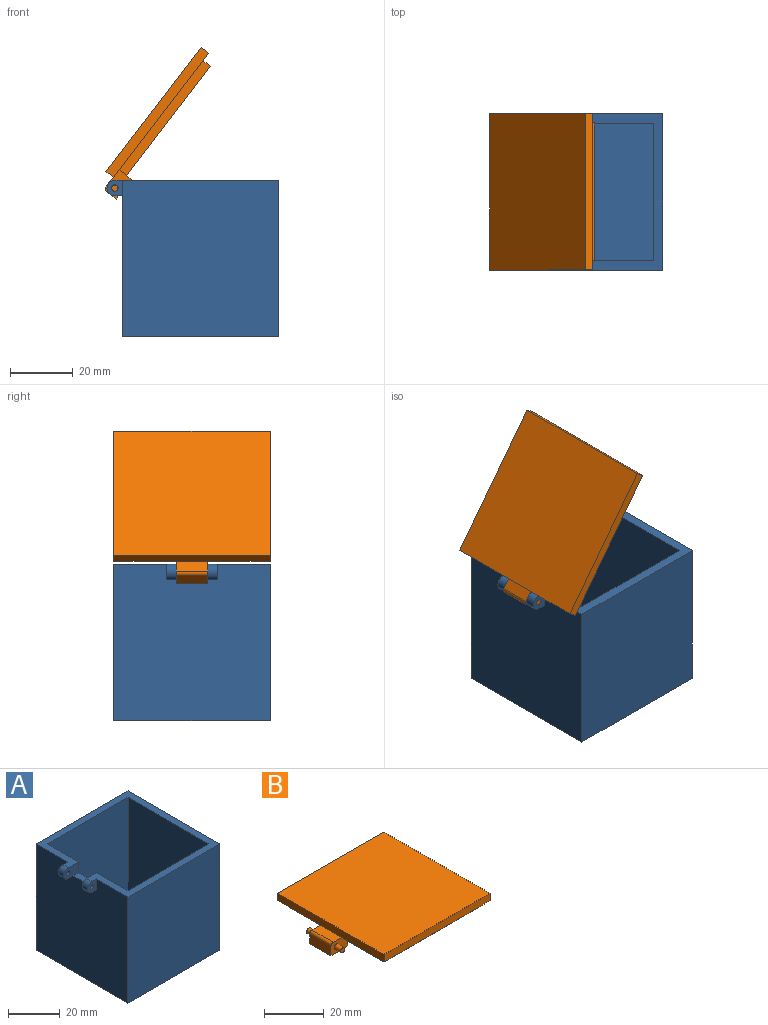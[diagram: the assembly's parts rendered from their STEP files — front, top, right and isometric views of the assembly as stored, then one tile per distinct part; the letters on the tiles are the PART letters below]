
ASSEMBLY  parts=2 mates=1
PART A: 22 faces, bbox 55x50x50 mm
  f0: plane 8x5mm, normal (0,-1,0), area 33.9mm2, adj f3,f4,f7,f16,f18,f21
  f1: plane 8x5mm, normal (0,1,0), area 33.9mm2, adj f3,f5,f7,f16,f19,f20
  f2: plane 5x5mm, normal (0,1,0), area 18.9mm2, adj f3,f4,f6,f18,f21
  f3: plane 52.5x50mm, normal (0,0,1), area 549mm2, adj f0,f1,f2,f6,f7,f8,f9,f10
  f4: plane 3x2.5mm, normal (0,0,-1), area 7.5mm2, adj f0,f2,f6,f18
  f5: plane 3x2.5mm, normal (0,0,-1), area 7.5mm2, adj f1,f6,f17,f19
  f6: plane 50x50mm, normal (-1,0,0), area 2420mm2, adj f2,f3,f4,f5,f8,f10,f11,f16
  f7: plane 47x44mm, normal (1,0,0), area 2018mm2, adj f0,f1,f3,f12,f14,f15,f16
  f8: plane 50x50mm, normal (0,-1,0), area 2500mm2, adj f3,f6,f9,f11
  f9: plane 50x50mm, normal (1,0,0), area 2500mm2, adj f3,f8,f10,f11
  f10: plane 50x50mm, normal (0,1,0), area 2500mm2, adj f3,f6,f9,f11
  f11: plane 50x50mm, normal (0,0,-1), area 2500mm2, adj f6,f8,f9,f10
  f12: plane 47x44mm, normal (0,1,0), area 2068mm2, adj f3,f7,f13,f15
  f13: plane 47x44mm, normal (-1,0,0), area 2068mm2, adj f3,f12,f14,f15
  f14: plane 47x44mm, normal (0,-1,0), area 2068mm2, adj f3,f7,f13,f15
  f15: plane 44x44mm, normal (0,0,1), area 1936mm2, adj f7,f12,f13,f14
  f16: plane 10x3mm, normal (0,0,1), area 30mm2, adj f0,f1,f6,f7
  f17: plane 5x5mm, normal (0,-1,0), area 18.9mm2, adj f3,f5,f6,f19,f20
  f18: cylinder r=2.5mm len=5mm, axis (0,-1,0), area 23.6mm2, adj f0,f2,f3,f4
  f19: cylinder r=2.5mm len=5mm, axis (0,-1,0), area 23.6mm2, adj f1,f3,f5,f17
  f20: cylinder r=1.05mm len=3mm, axis (0,-1,0), area 19.8mm2, adj f1,f17
  f21: cylinder r=1.05mm len=3mm, axis (0,-1,0), area 19.8mm2, adj f0,f2
PART B: 23 faces, bbox 55x50x8 mm
  f0: plane 17x3mm, normal (-1,0,0), area 51mm2, adj f5,f8,f11,f14
  f1: plane 50x3mm, normal (-1,0,0), area 150mm2, adj f2,f4,f5,f6,f12
  f2: plane 50x3mm, normal (0,-1,0), area 150mm2, adj f1,f3,f5,f6
  f3: plane 50x3mm, normal (1,0,0), area 150mm2, adj f2,f4,f5,f6
  f4: plane 50x3mm, normal (0,1,0), area 150mm2, adj f1,f3,f5,f6
  f5: plane 50x50mm, normal (0,0,-1), area 534mm2, adj f0,f1,f2,f3,f4,f7,f8,f9
  f6: plane 50x50mm, normal (0,0,1), area 2500mm2, adj f1,f2,f3,f4
  f7: plane 44x3mm, normal (1,0,0), area 132mm2, adj f5,f8,f10,f11
  f8: plane 44x3mm, normal (0,-1,0), area 132mm2, adj f0,f5,f7,f11
  f9: plane 17x3mm, normal (-1,0,0), area 51mm2, adj f5,f10,f11,f16
  f10: plane 44x3mm, normal (0,1,0), area 132mm2, adj f5,f7,f9,f11
  f11: plane 44x44mm, normal (0,0,-1), area 1936mm2, adj f0,f7,f8,f9,f10,f13
  f12: plane 10x4mm, normal (0,0,1), area 40mm2, adj f1,f14,f16,f22
  f13: plane 10x2mm, normal (1,0,0), area 20mm2, adj f11,f14,f16,f17
  f14: plane 8x5mm, normal (0,-1,0), area 36.6mm2, adj f0,f5,f12,f13,f15,f17,f18,f22
  f15: plane 10x4mm, normal (-1,0,0), area 40mm2, adj f14,f16,f17,f22
  f16: plane 8x5mm, normal (0,1,0), area 36.6mm2, adj f5,f9,f12,f13,f15,f17,f20,f22
  f17: plane 10x8mm, normal (0,0,-1), area 80mm2, adj f13,f14,f15,f16
  f18: cylinder r=1mm len=3mm, axis (0,1,0), area 18.8mm2, adj f14,f19
  f19: plane 2x2mm, normal (0,-1,0), area 3.1mm2, adj f18
  f20: cylinder r=1mm len=3mm, axis (0,-1,0), area 18.8mm2, adj f16,f21
  f21: plane 2x2mm, normal (0,1,0), area 3.1mm2, adj f20
  f22: cylinder r=1mm len=10mm, axis (0,1,0), area 15.7mm2, adj f12,f14,f15,f16
PLACE A t=(-9.34,-24.54,-4.86)mm fixed
PLACE B rot(axis=(0,-1,0),52.5deg) t=(-14.68,-24.54,47.98)mm
MATE revolute B.f18 <-> A.f18  axis (0,-1,0) through (-11.84,-7.54,42.64)mm
